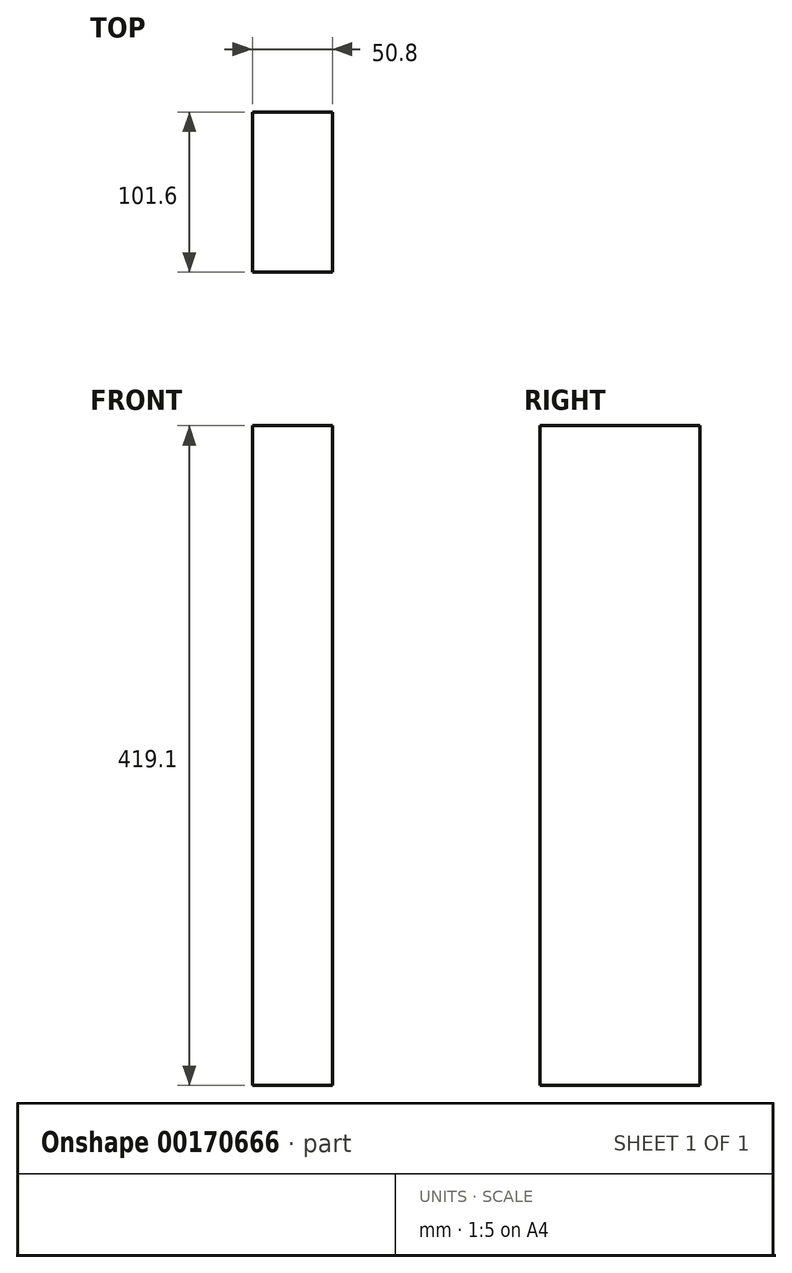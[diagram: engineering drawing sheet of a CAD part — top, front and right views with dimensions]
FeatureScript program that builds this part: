
annotation { "Feature Type Name" : "Feature", "Feature Type Description" : "" }
export const myFeature = defineFeature(function(context is Context, id is Id, definition is map)
    precondition{}
    {
        {
            var Q0;
            Q0=qCreatedBy(makeId("Top.planeOp"),FACE);
            var sketch = newSketch(context, id + "F0", { "sketchPlane" : qUnion([Q0])});
            skLineSegment(sketch, "E0.bottom", {"start": v(25.4, -50.8) * mm, "end": v(-25.4, -50.8) * mm});
            skLineSegment(sketch, "E0.top", {"start": v(25.4, 50.8) * mm, "end": v(-25.4, 50.8) * mm});
            skLineSegment(sketch, "E0.left", {"start": v(25.4, -50.8) * mm, "end": v(25.4, 50.8) * mm});
            skLineSegment(sketch, "E0.right", {"start": v(-25.4, -50.8) * mm, "end": v(-25.4, 50.8) * mm});
            skPoint(sketch, "E0.middle", {"position": v(0, 0) * mm});
            skSolve(sketch);
        }
        {
            var Q0;
            Q0 = qSketchRegion(id + "F0", true);
            extrude(context, id + "F1", {"entities" : qUnion([Q0]), "oppositeDirection" : true, "depth" : 419.1 * mm});
        }
    });
